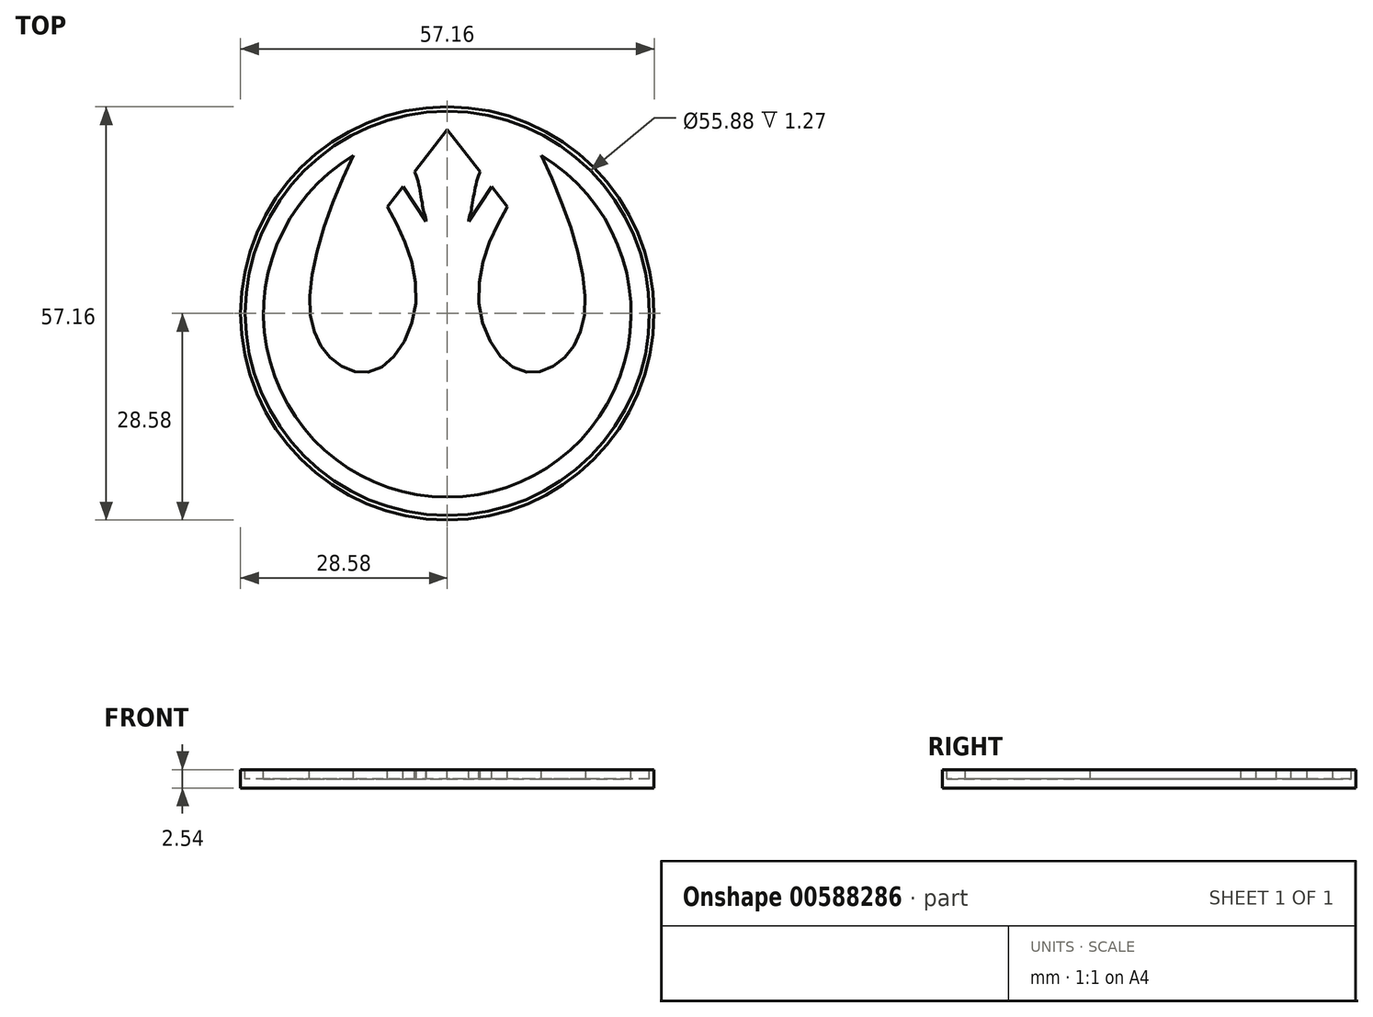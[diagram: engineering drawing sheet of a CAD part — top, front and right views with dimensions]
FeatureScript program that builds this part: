
annotation { "Feature Type Name" : "Feature", "Feature Type Description" : "" }
export const myFeature = defineFeature(function(context is Context, id is Id, definition is map)
    precondition{}
    {
        {
            var Q0;
            Q0=qCreatedBy(makeId("Top.planeOp"),FACE);
            var sketch = newSketch(context, id + "F0", { "sketchPlane" : qUnion([Q0])});
            skArc(sketch, "E0", {"start": v(0, 25.4) * mm, "mid": v(-25.4, 0) * mm, "end": v(0, -25.4) * mm});
            skLineSegment(sketch, "E1", {"start": v(0, 25.4) * mm, "end": v(0, -25.4) * mm});
            skLineSegment(sketch, "E2", {"start": v(-8.3, 14.77) * mm, "end": v(0, 25.4) * mm});
            skLineSegment(sketch, "E3", {"start": v(-6.12, 17.56) * mm, "end": v(-2.97, 12.7) * mm});
            skFitSpline(sketch, "E4", {"points": [v(-4.53, 19.6) * mm, v(-3.22, 13.9) * mm, v(-2.97, 12.7) * mm], "startDerivative": vector(3.24, -6.13) * mm, "endDerivative": vector(-0.1, -7.65) * mm});
            skFitSpline(sketch, "E5", {"points": [v(-12.98, 21.83) * mm, v(-19.05, 2) * mm, v(-15.99, -6.3) * mm, v(-9.93, -7.87) * mm, v(-4.38, 1.25) * mm, v(-8.3, 14.77) * mm], "startDerivative": vector(-33.92, -70.48) * mm, "endDerivative": vector(-30.58, 50.45) * mm});
            skLineSegment(sketch, "E6.MirrorCS", {"start": v(6.12, 17.56) * mm, "end": v(2.97, 12.7) * mm});
            skFitSpline(sketch, "E7.MirrorCS", {"points": [v(4.53, 19.6) * mm, v(3.22, 13.9) * mm, v(2.97, 12.7) * mm], "startDerivative": vector(-3.24, -6.13) * mm, "endDerivative": vector(0.1, -7.65) * mm});
            skLineSegment(sketch, "E8.MirrorCS", {"start": v(8.3, 14.77) * mm, "end": v(0, 25.4) * mm});
            skArc(sketch, "E9.MirrorCS", {"start": v(0, 25.4) * mm, "mid": v(25.4, 0) * mm, "end": v(0, -25.4) * mm});
            skFitSpline(sketch, "E10.MirrorCS", {"points": [v(12.98, 21.83) * mm, v(19.05, 2) * mm, v(15.99, -6.3) * mm, v(9.93, -7.87) * mm, v(4.38, 1.25) * mm, v(8.3, 14.77) * mm], "startDerivative": vector(33.92, -70.48) * mm, "endDerivative": vector(30.58, 50.45) * mm});
            skCircle(sketch, "E11", {"center": v(0, 0) * mm, "radius": 27.94 * mm});
            skSolve(sketch);
        }
        {
            var Q0;
            Q0=qCreatedBy(makeId("Top.planeOp"),FACE);
            var sketch = newSketch(context, id + "F1", { "sketchPlane" : qUnion([Q0])});
            skCircle(sketch, "E12", {"center": v(0, 0) * mm, "radius": 28.57 * mm});
            skSolve(sketch);
        }
        {
            var Q0;
            Q0=makeQuery(id+"F1.imprint","IMPRINT",FACE,{"disambiguationData":[TD([[makeQuery(id+"F1.imprint","IMPRINT",EDGE,{"derivedFrom":sQuery(id+"F1.wireOp",EDGE,"E12")}),1.0]])]});
            extrude(context, id + "F2", {"entities" : qUnion([Q0]), "oppositeDirection" : true, "depth" : 2.54 * mm, "offsetDistance" : 25.4 * mm});
        }
        {
            var Q0;
            {var subQ5=sQuery(id+"F0.wireOp",EDGE,"E5");Q0=makeQuery(id+"F0.imprint","IMPRINT",FACE,{"disambiguationData":[TD([[makeQuery(id+"F0.imprint","IMPRINT",EDGE,{"derivedFrom":subQ5}),1.0]])]});}
            var Q1;
            {var subQ3=sQuery(id+"F0.wireOp",EDGE,"E10.MirrorCS");Q1=makeQuery(id+"F0.imprint","IMPRINT",FACE,{"disambiguationData":[TD([[makeQuery(id+"F0.imprint","IMPRINT",EDGE,{"derivedFrom":subQ3}),-1.0]])]});}
            var Q2;
            Q2=makeQuery(id+"F0.imprint","IMPRINT",FACE,{"disambiguationData":[TD([[makeQuery(id+"F0.imprint","IMPRINT",EDGE,{"derivedFrom":sQuery(id+"F0.wireOp",EDGE,"E11")}),1.0]])]});
            var Q3;
            {var subQ0=sQuery(id+"F0.wireOp",EDGE,"E6.MirrorCS");Q3=makeQuery(id+"F0.imprint","IMPRINT",FACE,{"disambiguationData":[TD([[makeQuery(id+"F0.imprint","IMPRINT",EDGE,{"derivedFrom":subQ0}),-1.0]])]});}
            var Q4;
            {var subQ0=sQuery(id+"F0.wireOp",EDGE,"E3");Q4=makeQuery(id+"F0.imprint","IMPRINT",FACE,{"disambiguationData":[TD([[makeQuery(id+"F0.imprint","IMPRINT",EDGE,{"derivedFrom":subQ0}),1.0]])]});}
            extrude(context, id + "F3", {"entities" : qUnion([Q0, Q1, Q2, Q3, Q4]), "operationType" : NewBodyOperationType.REMOVE, "oppositeDirection" : true, "depth" : 1.27 * mm, "offsetDistance" : 25.4 * mm});
        }
    });
